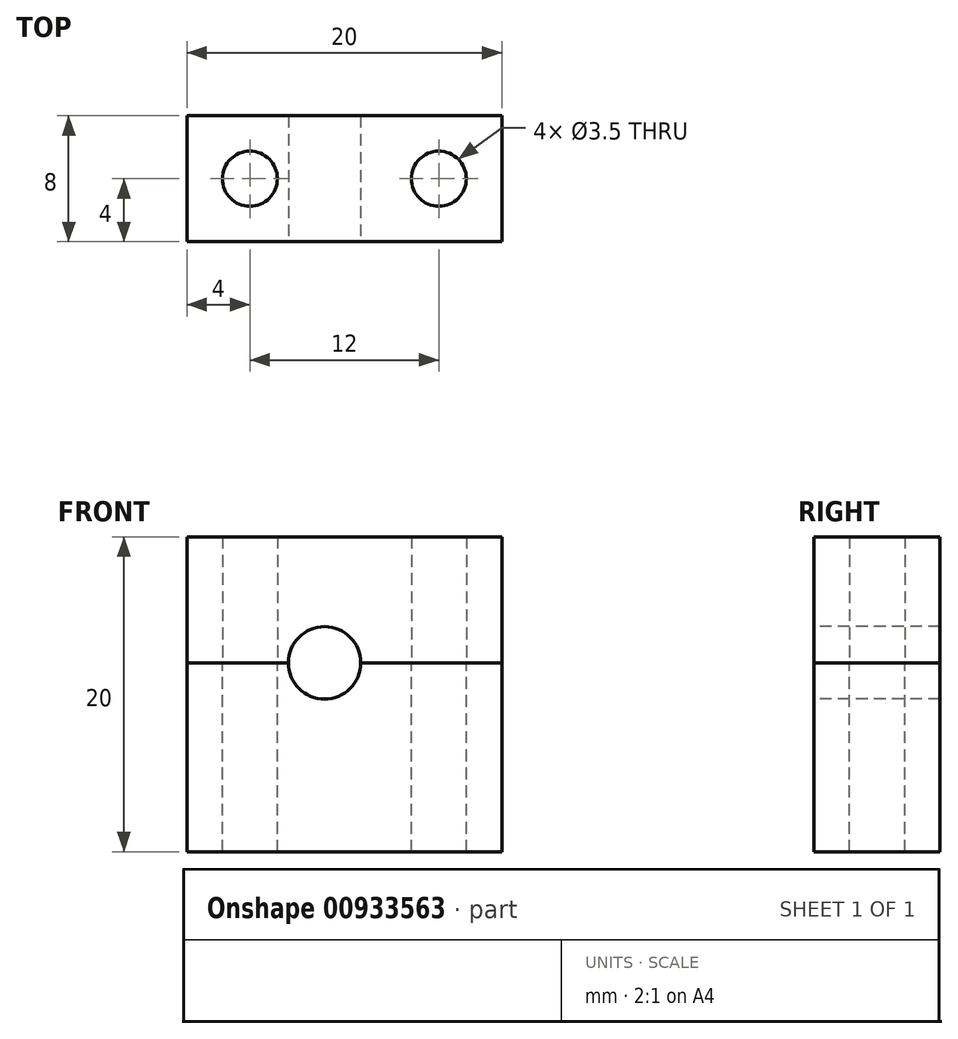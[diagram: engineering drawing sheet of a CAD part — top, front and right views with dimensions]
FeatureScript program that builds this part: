
annotation { "Feature Type Name" : "Feature", "Feature Type Description" : "" }
export const myFeature = defineFeature(function(context is Context, id is Id, definition is map)
    precondition{}
    {
        {
            var Q0;
            Q0=qCreatedBy(makeId("Top.planeOp"),FACE);
            var sketch = newSketch(context, id + "F0", { "sketchPlane" : qUnion([Q0])});
            skPoint(sketch, "E0", {"position": v(-6, 0) * mm});
            skPoint(sketch, "E1", {"position": v(6, 0) * mm});
            skLineSegment(sketch, "E2.bottom", {"start": v(10, -4) * mm, "end": v(-10, -4) * mm});
            skLineSegment(sketch, "E2.top", {"start": v(10, 4) * mm, "end": v(-10, 4) * mm});
            skLineSegment(sketch, "E2.left", {"start": v(10, -4) * mm, "end": v(10, 4) * mm});
            skLineSegment(sketch, "E2.right", {"start": v(-10, -4) * mm, "end": v(-10, 4) * mm});
            skSolve(sketch);
        }
        {
            var Q0;
            Q0=makeQuery(id+"F0.imprint","IMPRINT",FACE,{"disambiguationData":[TD([[makeQuery(id+"F0.imprint","IMPRINT",EDGE,{"derivedFrom":sQuery(id+"F0.wireOp",EDGE,"E2.bottom")}),-1.0]])]});
            extrude(context, id + "F1", {"entities" : qUnion([Q0]), "oppositeDirection" : true, "depth" : 12 * mm, "offsetDistance" : 25 * mm});
        }
        {
            var Q0;
            Q0=sQuery(id+"F0.wireOp",VERTEX,"E1");
            var Q1;
            Q1=sQuery(id+"F0.wireOp",VERTEX,"E0");
            var Q2;
            Q2=makeQuery(id+"F1.opExtrude","SWEPT_BODY",BODY,{"disambiguationData":[OSD([sQuery(id+"F0.wireOp",EDGE,"E2.bottom"),sQuery(id+"F0.wireOp",EDGE,"E2.top"),sQuery(id+"F0.wireOp",EDGE,"E2.left"),sQuery(id+"F0.wireOp",EDGE,"E2.right")])]});
            hole(context, id + "F2", {"style" : HoleStyle.SIMPLE, "endStyle" : HoleEndStyle.THROUGH, "holeDiameter" : 3.5 * mm, "majorDiameter" : 3 * mm, "isTappedThrough" : true, "tappedDepth" : 12 * mm, "tapClearance" : 3, "startFromSketch" : true, "locations" : qUnion([Q0, Q1]), "scope" : qUnion([Q2])});
        }
        {
            var Q0;
            Q0=makeQuery(id+"F0.imprint","IMPRINT",FACE,{"disambiguationData":[TD([[makeQuery(id+"F0.imprint","IMPRINT",EDGE,{"derivedFrom":sQuery(id+"F0.wireOp",EDGE,"E2.bottom")}),-1.0]])]});
            extrude(context, id + "F3", {"entities" : qUnion([Q0]), "depth" : 8 * mm, "offsetDistance" : 25 * mm});
        }
        {
            var Q0;
            Q0=sQuery(id+"F0.wireOp",VERTEX,"E0");
            var Q1;
            Q1=sQuery(id+"F0.wireOp",VERTEX,"E1");
            var Q2;
            Q2=makeQuery(id+"F3.opExtrude","SWEPT_BODY",BODY,{"disambiguationData":[OSD([sQuery(id+"F0.wireOp",EDGE,"E2.bottom"),sQuery(id+"F0.wireOp",EDGE,"E2.top"),sQuery(id+"F0.wireOp",EDGE,"E2.left"),sQuery(id+"F0.wireOp",EDGE,"E2.right")])]});
            hole(context, id + "F4", {"style" : HoleStyle.SIMPLE, "endStyle" : HoleEndStyle.THROUGH, "oppositeDirection" : true, "holeDiameter" : 3.5 * mm, "majorDiameter" : 5 * mm, "isTappedThrough" : true, "tappedDepth" : 12 * mm, "tapClearance" : 3, "startFromSketch" : true, "locations" : qUnion([Q0, Q1]), "scope" : qUnion([Q2])});
        }
        {
            var Q0;
            Q0=makeQuery(id+"F3.opExtrude","SWEPT_FACE",FACE,{"disambiguationData":[OSD([sQuery(id+"F0.wireOp",EDGE,"E2.bottom")])]});
            var sketch = newSketch(context, id + "F5", { "sketchPlane" : qUnion([Q0])});
            skPoint(sketch, "E3", {"position": v(-1.26, 0) * mm});
            skSolve(sketch);
        }
        {
            var Q0;
            Q0=sQuery(id+"F5.wireOp",VERTEX,"E3");
            var Q1;
            Q1=makeQuery(id+"F1.opExtrude","SWEPT_BODY",BODY,{"disambiguationData":[OSD([sQuery(id+"F0.wireOp",EDGE,"E2.bottom"),sQuery(id+"F0.wireOp",EDGE,"E2.top"),sQuery(id+"F0.wireOp",EDGE,"E2.left"),sQuery(id+"F0.wireOp",EDGE,"E2.right")])]});
            var Q2;
            Q2=makeQuery(id+"F3.opExtrude","SWEPT_BODY",BODY,{"disambiguationData":[OSD([sQuery(id+"F0.wireOp",EDGE,"E2.bottom"),sQuery(id+"F0.wireOp",EDGE,"E2.top"),sQuery(id+"F0.wireOp",EDGE,"E2.left"),sQuery(id+"F0.wireOp",EDGE,"E2.right")])]});
            hole(context, id + "F6", {"style" : HoleStyle.SIMPLE, "endStyle" : HoleEndStyle.THROUGH, "holeDiameter" : 4.6 * mm, "majorDiameter" : 5 * mm, "isTappedThrough" : true, "tappedDepth" : 12 * mm, "tapClearance" : 3, "startFromSketch" : true, "locations" : qUnion([Q0]), "scope" : qUnion([Q1, Q2])});
        }
    });
